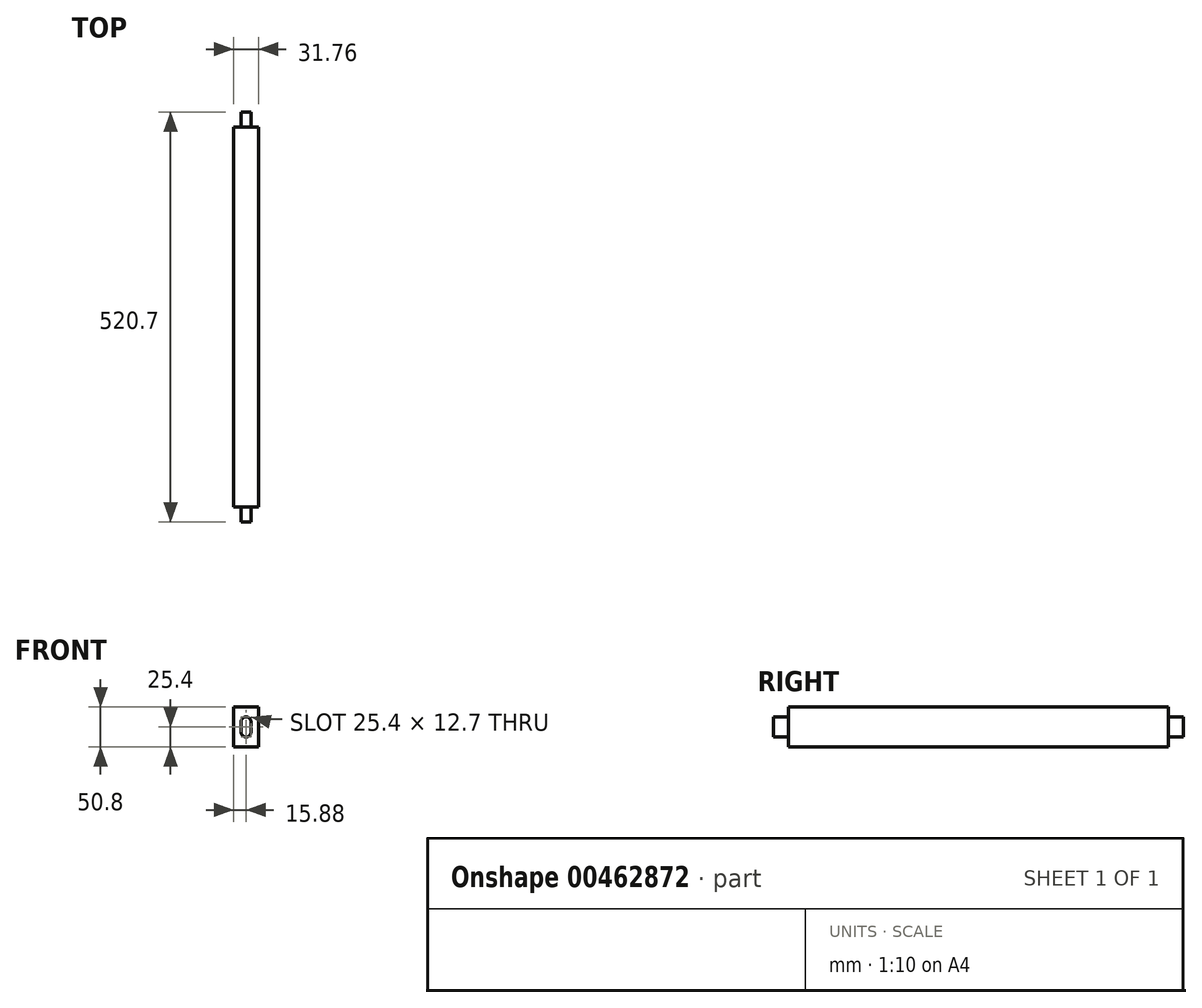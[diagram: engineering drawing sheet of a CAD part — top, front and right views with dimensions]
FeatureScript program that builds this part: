
annotation { "Feature Type Name" : "Feature", "Feature Type Description" : "" }
export const myFeature = defineFeature(function(context is Context, id is Id, definition is map)
    precondition{}
    {
        {
            var Q0;
            Q0=qCreatedBy(makeId("Front.planeOp"),FACE);
            var sketch = newSketch(context, id + "F0", { "sketchPlane" : qUnion([Q0])});
            skLineSegment(sketch, "E0.bottom", {"start": v(-15.88, -25.4) * mm, "end": v(15.88, -25.4) * mm});
            skLineSegment(sketch, "E0.top", {"start": v(-15.87, 25.4) * mm, "end": v(15.88, 25.4) * mm});
            skLineSegment(sketch, "E0.left", {"start": v(-15.88, -25.4) * mm, "end": v(-15.87, 25.4) * mm});
            skLineSegment(sketch, "E0.right", {"start": v(15.88, -25.4) * mm, "end": v(15.88, 25.4) * mm});
            skLineSegment(sketch, "E1", {"start": v(-15.88, -25.4) * mm, "end": v(15.88, 25.4) * mm, "construction": true});
            skSolve(sketch);
        }
        {
            var Q0;
            Q0=makeQuery(id+"F0.imprint","IMPRINT",FACE,{"disambiguationData":[TD([[makeQuery(id+"F0.imprint","IMPRINT",EDGE,{"derivedFrom":sQuery(id+"F0.wireOp",EDGE,"E0.bottom")}),1.0]])]});
            extrude(context, id + "F1", {"entities" : qUnion([Q0]), "depth" : 482.6 * mm});
        }
        {
            var Q0;
            Q0=makeQuery(id+"F1.opExtrude","CAP_FACE",FACE,{"disambiguationData":[OSD([sQuery(id+"F0.wireOp",EDGE,"E0.bottom"),sQuery(id+"F0.wireOp",EDGE,"E0.top"),sQuery(id+"F0.wireOp",EDGE,"E0.left"),sQuery(id+"F0.wireOp",EDGE,"E0.right")])],"isStart":true});
            var sketch = newSketch(context, id + "F2", { "sketchPlane" : qUnion([Q0])});
            skLineSegment(sketch, "E2.bottom", {"start": v(-6.35, -6.35) * mm, "end": v(6.35, -6.35) * mm, "construction": true});
            skLineSegment(sketch, "E2.top", {"start": v(-6.35, 6.35) * mm, "end": v(6.35, 6.35) * mm, "construction": true});
            skLineSegment(sketch, "E2.left", {"start": v(-6.35, -6.35) * mm, "end": v(-6.35, 6.35) * mm});
            skLineSegment(sketch, "E2.right", {"start": v(6.35, -6.35) * mm, "end": v(6.35, 6.35) * mm});
            skArc(sketch, "E3", {"start": v(-6.35, 6.35) * mm, "mid": v(0, 12.7) * mm, "end": v(6.35, 6.35) * mm});
            skArc(sketch, "E4", {"start": v(6.35, -6.35) * mm, "mid": v(0, -12.7) * mm, "end": v(-6.35, -6.35) * mm});
            skLineSegment(sketch, "E5", {"start": v(0, 6.35) * mm, "end": v(0, -6.35) * mm, "construction": true});
            skSolve(sketch);
        }
        {
            var Q0;
            Q0 = qSketchRegion(id + "F2", true);
            extrude(context, id + "F3", {"entities" : qUnion([Q0]), "operationType" : NewBodyOperationType.ADD, "depth" : 19.05 * mm});
        }
        {
            var Q0;
            Q0=makeQuery(id+"F1.opExtrude","CAP_FACE",FACE,{"disambiguationData":[OSD([sQuery(id+"F0.wireOp",EDGE,"E0.bottom"),sQuery(id+"F0.wireOp",EDGE,"E0.top"),sQuery(id+"F0.wireOp",EDGE,"E0.left"),sQuery(id+"F0.wireOp",EDGE,"E0.right")])],"isStart":false});
            var sketch = newSketch(context, id + "F4", { "sketchPlane" : qUnion([Q0])});
            skLineSegment(sketch, "E6.bottom", {"start": v(-6.35, -6.35) * mm, "end": v(6.35, -6.35) * mm, "construction": true});
            skLineSegment(sketch, "E6.top", {"start": v(-6.35, 6.35) * mm, "end": v(6.35, 6.35) * mm, "construction": true});
            skLineSegment(sketch, "E6.left", {"start": v(-6.35, -6.35) * mm, "end": v(-6.35, 6.35) * mm});
            skLineSegment(sketch, "E6.right", {"start": v(6.35, -6.35) * mm, "end": v(6.35, 6.35) * mm});
            skArc(sketch, "E7", {"start": v(-6.35, 6.35) * mm, "mid": v(0, 12.7) * mm, "end": v(6.35, 6.35) * mm});
            skArc(sketch, "E8", {"start": v(6.35, -6.35) * mm, "mid": v(0, -12.7) * mm, "end": v(-6.35, -6.35) * mm});
            skLineSegment(sketch, "E9", {"start": v(0, 6.35) * mm, "end": v(0, -6.35) * mm, "construction": true});
            skSolve(sketch);
        }
        {
            var Q0;
            Q0 = qSketchRegion(id + "F4", true);
            extrude(context, id + "F5", {"entities" : qUnion([Q0]), "operationType" : NewBodyOperationType.ADD, "depth" : 19.05 * mm});
        }
    });
